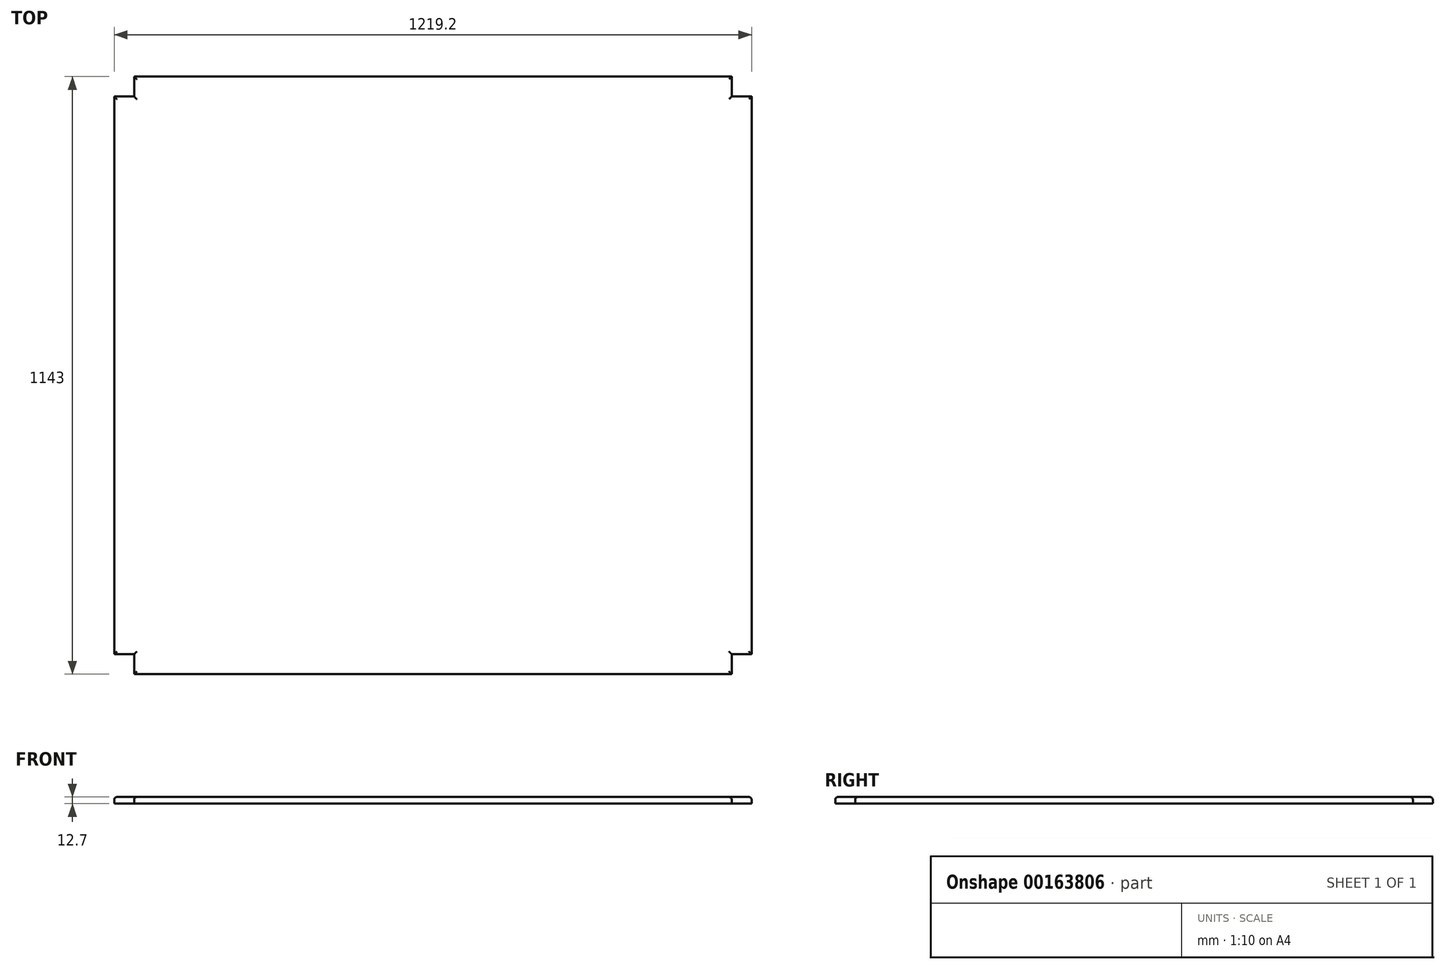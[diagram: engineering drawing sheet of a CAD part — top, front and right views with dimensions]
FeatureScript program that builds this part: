
annotation { "Feature Type Name" : "Feature", "Feature Type Description" : "" }
export const myFeature = defineFeature(function(context is Context, id is Id, definition is map)
    precondition{}
    {
        {
            var Q0;
            Q0=qCreatedBy(makeId("Top.planeOp"),FACE);
            var sketch = newSketch(context, id + "F0", { "sketchPlane" : qUnion([Q0])});
            skLineSegment(sketch, "E0.bottom", {"start": v(571.5, -571.5) * mm, "end": v(-571.5, -571.5) * mm});
            skLineSegment(sketch, "E0.top", {"start": v(571.5, 571.5) * mm, "end": v(-571.5, 571.5) * mm});
            skLineSegment(sketch, "E0.left", {"start": v(609.6, -533.4) * mm, "end": v(609.6, 533.4) * mm});
            skLineSegment(sketch, "E0.right", {"start": v(-609.6, -533.4) * mm, "end": v(-609.6, 533.4) * mm});
            skPoint(sketch, "E0.middle", {"position": v(0, 0) * mm});
            skLineSegment(sketch, "E1.top", {"start": v(-609.6, -533.4) * mm, "end": v(-571.5, -533.4) * mm});
            skLineSegment(sketch, "E1.right", {"start": v(-571.5, -571.5) * mm, "end": v(-571.5, -533.4) * mm});
            skLineSegment(sketch, "E2", {"start": v(0, 0) * mm, "end": v(228.97, 0) * mm, "construction": true});
            skLineSegment(sketch, "E3", {"start": v(0, 0) * mm, "end": v(0, 147.96) * mm, "construction": true});
            skLineSegment(sketch, "E4.MirrorCS", {"start": v(609.6, -533.4) * mm, "end": v(571.5, -533.4) * mm});
            skLineSegment(sketch, "E5.MirrorCS", {"start": v(571.5, -571.5) * mm, "end": v(571.5, -533.4) * mm});
            skLineSegment(sketch, "E6.MirrorCS", {"start": v(-609.6, 533.4) * mm, "end": v(-571.5, 533.4) * mm});
            skLineSegment(sketch, "E7.MirrorCS", {"start": v(-571.5, 571.5) * mm, "end": v(-571.5, 533.4) * mm});
            skLineSegment(sketch, "E8.MirrorCS", {"start": v(571.5, 571.5) * mm, "end": v(571.5, 533.4) * mm});
            skLineSegment(sketch, "E9.MirrorCS", {"start": v(609.6, 533.4) * mm, "end": v(571.5, 533.4) * mm});
            skSolve(sketch);
        }
        {
            var Q0;
            Q0=qSketchRegion(id+"F0",true);
            extrude(context, id + "F1", {"entities" : qUnion([Q0]), "depth" : 12.7 * mm});
        }
        {
            var Q0;
            Q0=makeQuery(id+"F1.opExtrude","CAP_FACE",FACE,{"disambiguationData":[OSD([sQuery(id+"F0.wireOp",EDGE,"GFZXVJBh-xqXL-qb6E-FtNm-0ZqrcdShkxDp.bottom"),sQuery(id+"F0.wireOp",EDGE,"GFZXVJBh-xqXL-qb6E-FtNm-0ZqrcdShkxDp.top"),sQuery(id+"F0.wireOp",EDGE,"GFZXVJBh-xqXL-qb6E-FtNm-0ZqrcdShkxDp.left"),sQuery(id+"F0.wireOp",EDGE,"GFZXVJBh-xqXL-qb6E-FtNm-0ZqrcdShkxDp.right"),sQuery(id+"F0.wireOp",EDGE,"b15ae54a-3f8c-4f60-8baa-cd31eb437c6e.filletArc"),sQuery(id+"F0.wireOp",EDGE,"aa749b1a-4f62-40e5-a9dd-a47ec50e650c.filletArc"),sQuery(id+"F0.wireOp",EDGE,"2b33ca63-df12-433b-986b-ef48bfc9de00.filletArc"),sQuery(id+"F0.wireOp",EDGE,"b19e8cbf-3efd-47e7-9b03-fc77b71e0aba.filletArc")])],"isStart":false});
            var Q1;
            Q1=makeQuery(id+"F1.opExtrude","CAP_FACE",FACE,{"disambiguationData":[OSD([sQuery(id+"F0.wireOp",EDGE,"E0.bottom"),sQuery(id+"F0.wireOp",EDGE,"E0.top"),sQuery(id+"F0.wireOp",EDGE,"E0.left"),sQuery(id+"F0.wireOp",EDGE,"E0.right"),sQuery(id+"F0.wireOp",EDGE,"E1.top"),sQuery(id+"F0.wireOp",EDGE,"E1.right"),sQuery(id+"F0.wireOp",EDGE,"E4.MirrorCS"),sQuery(id+"F0.wireOp",EDGE,"E5.MirrorCS"),sQuery(id+"F0.wireOp",EDGE,"E6.MirrorCS"),sQuery(id+"F0.wireOp",EDGE,"E7.MirrorCS"),sQuery(id+"F0.wireOp",EDGE,"E8.MirrorCS"),sQuery(id+"F0.wireOp",EDGE,"E9.MirrorCS")])],"isStart":false});
            fillet(context, id + "F2", {"entities" : qUnion([Q0, Q1]), "radius" : 5.08 * mm, "tangentPropagation" : true, "allowEdgeOverflow" : false});
        }
    });
